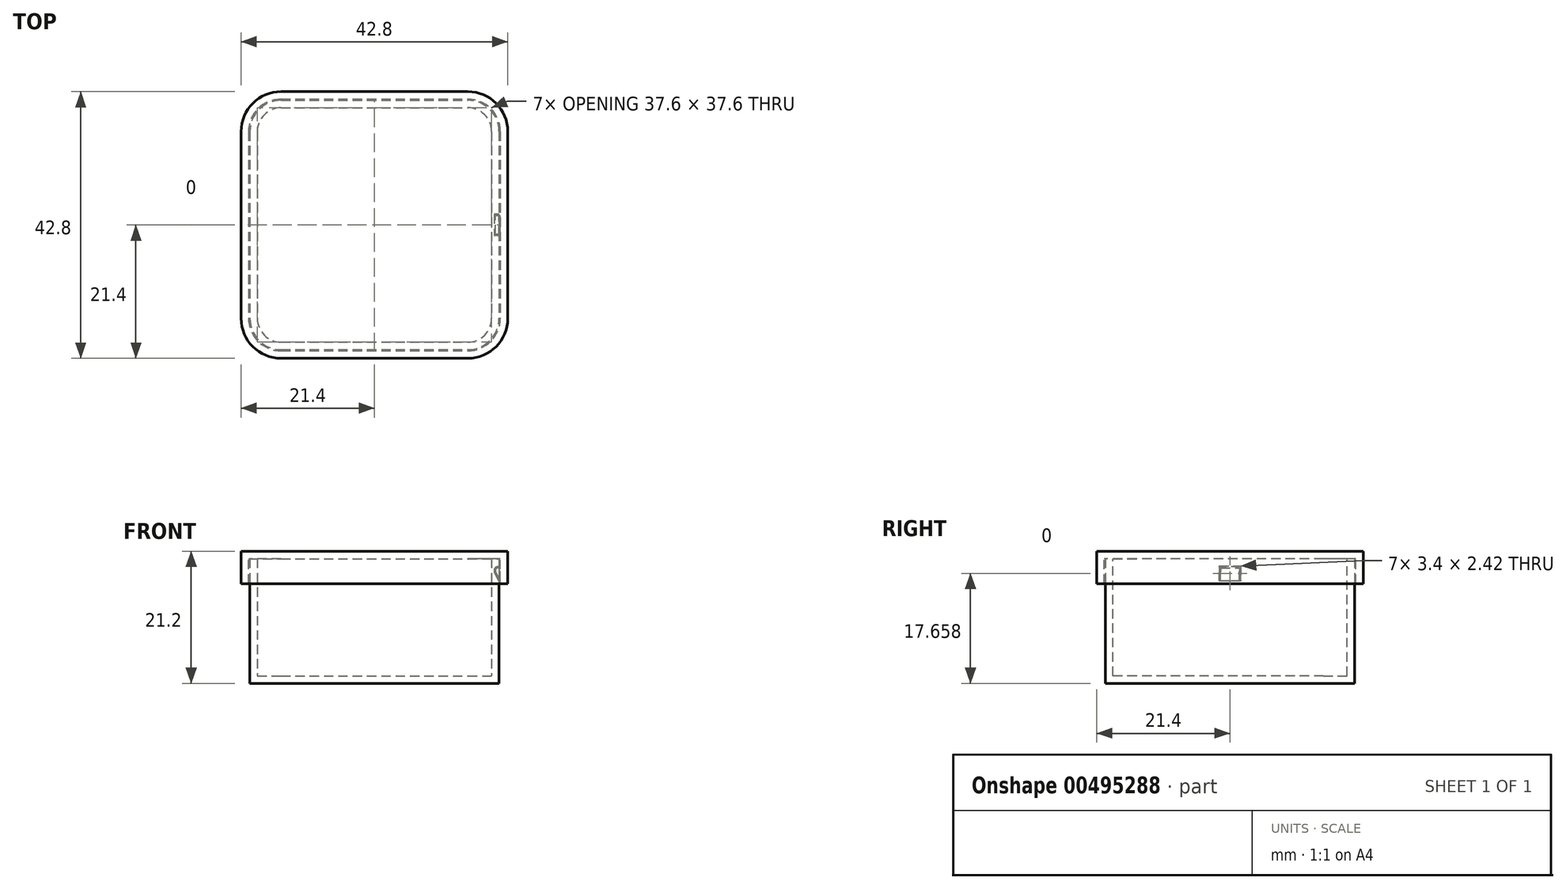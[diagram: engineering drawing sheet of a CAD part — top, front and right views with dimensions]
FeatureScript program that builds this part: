
annotation { "Feature Type Name" : "Feature", "Feature Type Description" : "" }
export const myFeature = defineFeature(function(context is Context, id is Id, definition is map)
    precondition{}
    {
        {
            var Q0;
            Q0=qCreatedBy(makeId("Top.planeOp"),FACE);
            var sketch = newSketch(context, id + "F0", { "sketchPlane" : qUnion([Q0])});
            skLineSegment(sketch, "E0.bottom", {"start": v(-20, 20) * mm, "end": v(20, 20) * mm});
            skLineSegment(sketch, "E0.top", {"start": v(-20, -20) * mm, "end": v(20, -20) * mm});
            skLineSegment(sketch, "E0.left", {"start": v(-20, 20) * mm, "end": v(-20, -20) * mm});
            skLineSegment(sketch, "E0.right", {"start": v(20, 20) * mm, "end": v(20, -20) * mm});
            skPoint(sketch, "E0.middle", {"position": v(0, 0) * mm});
            skSolve(sketch);
        }
        {
            var Q0;
            Q0=qSketchRegion(id+"F0",true);
            extrude(context, id + "F1", {"entities" : qUnion([Q0]), "depth" : 20 * mm});
        }
        {
            var Q0;
            Q0=makeQuery(id+"F1.opExtrude","SWEPT_EDGE",EDGE,{"disambiguationData":[OSD([sQuery(id+"F0.wireOp",EDGE,"E0.top"),sQuery(id+"F0.wireOp",EDGE,"E0.right")])]});
            var Q1;
            Q1=makeQuery(id+"F1.opExtrude","SWEPT_EDGE",EDGE,{"disambiguationData":[OSD([sQuery(id+"F0.wireOp",EDGE,"E0.bottom"),sQuery(id+"F0.wireOp",EDGE,"E0.right")])]});
            var Q2;
            Q2=makeQuery(id+"F1.opExtrude","SWEPT_EDGE",EDGE,{"disambiguationData":[OSD([sQuery(id+"F0.wireOp",EDGE,"E0.top"),sQuery(id+"F0.wireOp",EDGE,"E0.left")])]});
            var Q3;
            Q3=makeQuery(id+"F1.opExtrude","SWEPT_EDGE",EDGE,{"disambiguationData":[OSD([sQuery(id+"F0.wireOp",EDGE,"E0.bottom"),sQuery(id+"F0.wireOp",EDGE,"E0.left")])]});
            fillet(context, id + "F2", {"entities" : qUnion([Q0, Q1, Q2, Q3]), "radius" : 5 * mm, "tangentPropagation" : true, "allowEdgeOverflow" : false});
        }
        {
            var Q0;
            Q0=makeQuery(id+"F1.opExtrude","CAP_FACE",FACE,{"disambiguationData":[OSD([sQuery(id+"F0.wireOp",EDGE,"E0.bottom"),sQuery(id+"F0.wireOp",EDGE,"E0.top"),sQuery(id+"F0.wireOp",EDGE,"E0.left"),sQuery(id+"F0.wireOp",EDGE,"E0.right")])],"isStart":false});
            shell(context, id + "F3", {"entities" : qUnion([Q0]), "thickness" : 1.2 * mm});
        }
        {
            var Q0;
            Q0=makeQuery(id+"F1.opExtrude","CAP_FACE",FACE,{"disambiguationData":[OSD([sQuery(id+"F0.wireOp",EDGE,"E0.bottom"),sQuery(id+"F0.wireOp",EDGE,"E0.top"),sQuery(id+"F0.wireOp",EDGE,"E0.left"),sQuery(id+"F0.wireOp",EDGE,"E0.right")])],"isStart":false});
            var sketch = newSketch(context, id + "F4", { "sketchPlane" : qUnion([Q0])});
            skLineSegment(sketch, "E1.0", {"start": v(-15, -20) * mm, "end": v(15, -20) * mm});
            skArc(sketch, "E1.1", {"start": v(15, -20) * mm, "mid": v(18.54, -18.54) * mm, "end": v(20, -15) * mm});
            skLineSegment(sketch, "E1.2", {"start": v(20, 15) * mm, "end": v(20, -15) * mm});
            skArc(sketch, "E1.3", {"start": v(20, 15) * mm, "mid": v(18.54, 18.54) * mm, "end": v(15, 20) * mm});
            skLineSegment(sketch, "E1.4", {"start": v(-15, 20) * mm, "end": v(15, 20) * mm});
            skArc(sketch, "E1.5", {"start": v(-15, 20) * mm, "mid": v(-18.54, 18.54) * mm, "end": v(-20, 15) * mm});
            skLineSegment(sketch, "E1.6", {"start": v(-20, 15) * mm, "end": v(-20, -15) * mm});
            skArc(sketch, "E1.7", {"start": v(-20, -15) * mm, "mid": v(-18.54, -18.54) * mm, "end": v(-15, -20) * mm});
            skArc(sketch, "E2.0", {"start": v(-20.2, -15) * mm, "mid": v(-18.68, -18.68) * mm, "end": v(-15, -20.2) * mm});
            skLineSegment(sketch, "E2.1", {"start": v(-20.2, 15) * mm, "end": v(-20.2, -15) * mm});
            skLineSegment(sketch, "E2.2", {"start": v(-15, -20.2) * mm, "end": v(15, -20.2) * mm});
            skArc(sketch, "E2.3", {"start": v(-15, 20.2) * mm, "mid": v(-18.68, 18.68) * mm, "end": v(-20.2, 15) * mm});
            skArc(sketch, "E2.4", {"start": v(15, -20.2) * mm, "mid": v(18.68, -18.68) * mm, "end": v(20.2, -15) * mm});
            skLineSegment(sketch, "E2.5", {"start": v(20.2, 15) * mm, "end": v(20.2, -15) * mm});
            skArc(sketch, "E2.6", {"start": v(20.2, 15) * mm, "mid": v(18.68, 18.68) * mm, "end": v(15, 20.2) * mm});
            skLineSegment(sketch, "E2.7", {"start": v(-15, 20.2) * mm, "end": v(15, 20.2) * mm});
            skArc(sketch, "E3.0", {"start": v(-21.4, -15) * mm, "mid": v(-19.53, -19.53) * mm, "end": v(-15, -21.4) * mm});
            skLineSegment(sketch, "E3.1", {"start": v(-21.4, 15) * mm, "end": v(-21.4, -15) * mm});
            skLineSegment(sketch, "E3.2", {"start": v(-15, -21.4) * mm, "end": v(15, -21.4) * mm});
            skArc(sketch, "E3.3", {"start": v(-15, 21.4) * mm, "mid": v(-19.53, 19.53) * mm, "end": v(-21.4, 15) * mm});
            skArc(sketch, "E3.4", {"start": v(15, -21.4) * mm, "mid": v(19.53, -19.53) * mm, "end": v(21.4, -15) * mm});
            skLineSegment(sketch, "E3.5", {"start": v(21.4, 15) * mm, "end": v(21.4, -15) * mm});
            skArc(sketch, "E3.6", {"start": v(21.4, 15) * mm, "mid": v(19.53, 19.53) * mm, "end": v(15, 21.4) * mm});
            skLineSegment(sketch, "E3.7", {"start": v(-15, 21.4) * mm, "end": v(15, 21.4) * mm});
            skSolve(sketch);
        }
        {
            var Q0;
            Q0=makeQuery(id+"F4.imprint","IMPRINT",FACE,{"disambiguationData":[TD([[makeQuery(id+"F4.imprint","IMPRINT",EDGE,{"derivedFrom":sQuery(id+"F4.wireOp",EDGE,"E2.0")}),-1.0]])]});
            var Q1;
            {var subQ3=sQuery(id+"F0.wireOp",EDGE,"E0.bottom");Q1=makeQuery(id+"F4.imprint","IMPRINT",FACE,{"disambiguationData":[TD([[makeQuery(id+"F4.imprint","IMPRINT",EDGE,{"derivedFrom":makeQuery(id+"F3.opShell","OFFSET_EDGE",EDGE,{"disambiguationData":[OSD([subQ3]),TDD([makeQuery(id+"F1.opExtrude","CAP_EDGE",EDGE,{"disambiguationData":[OSD([subQ3])],"isStart":false})])]})}),-1.0]])]});}
            var Q2;
            Q2=makeQuery(id+"F4.imprint","IMPRINT",FACE,{"disambiguationData":[TD([[makeQuery(id+"F4.imprint","IMPRINT",EDGE,{"derivedFrom":sQuery(id+"F4.wireOp",EDGE,"E1.0")}),1.0]])]});
            var Q3;
            Q3=makeQuery(id+"F4.imprint","IMPRINT",FACE,{"disambiguationData":[TD([[makeQuery(id+"F4.imprint","IMPRINT",EDGE,{"derivedFrom":sQuery(id+"F4.wireOp",EDGE,"E1.0")}),-1.0]])]});
            extrude(context, id + "F5", {"entities" : qUnion([Q0, Q1, Q2, Q3]), "depth" : 1.2 * mm});
        }
        {
            var Q0;
            Q0=makeQuery(id+"F4.imprint","IMPRINT",FACE,{"disambiguationData":[TD([[makeQuery(id+"F4.imprint","IMPRINT",EDGE,{"derivedFrom":sQuery(id+"F4.wireOp",EDGE,"E2.0")}),-1.0]])]});
            extrude(context, id + "F6", {"entities" : qUnion([Q0]), "operationType" : NewBodyOperationType.ADD, "oppositeDirection" : true, "depth" : 4 * mm});
        }
        {
            var Q0;
            Q0=qCreatedBy(makeId("Front.planeOp"),FACE);
            var sketch = newSketch(context, id + "F7", { "sketchPlane" : qUnion([Q0])});
            skLineSegment(sketch, "E4", {"start": v(20.2, 16.5) * mm, "end": v(20.2, 18.5) * mm});
            skLineSegment(sketch, "E5", {"start": v(20.2, 18.5) * mm, "end": v(19.8, 18.5) * mm});
            skLineSegment(sketch, "E6", {"start": v(20.2, 16.5) * mm, "end": v(19.45, 17.91) * mm});
            skArc(sketch, "E7", {"start": v(19.8, 18.5) * mm, "mid": v(19.46, 18.3) * mm, "end": v(19.45, 17.91) * mm});
            skArc(sketch, "E8", {"start": v(19.8, 18.5) * mm, "mid": v(20.08, 18.62) * mm, "end": v(20.2, 18.9) * mm});
            skLineSegment(sketch, "E9", {"start": v(20.2, 18.5) * mm, "end": v(19.4, 18.5) * mm, "construction": true});
            skLineSegment(sketch, "E10", {"start": v(20.2, 18.5) * mm, "end": v(20.2, 18.9) * mm});
            skArc(sketch, "E11.0", {"start": v(19.8, 18.7) * mm, "mid": v(19.92, 18.74) * mm, "end": v(19.99, 18.84) * mm});
            skArc(sketch, "E11.1", {"start": v(19.8, 18.7) * mm, "mid": v(19.29, 18.4) * mm, "end": v(19.27, 17.82) * mm});
            skLineSegment(sketch, "E11.2", {"start": v(20.2, 16.08) * mm, "end": v(19.27, 17.82) * mm});
            skLineSegment(sketch, "E12", {"start": v(19.99, 18.84) * mm, "end": v(20.2, 19.45) * mm});
            skLineSegment(sketch, "E13", {"start": v(20.2, 18.9) * mm, "end": v(20.2, 20) * mm});
            skLineSegment(sketch, "E14", {"start": v(20.2, 16.5) * mm, "end": v(20.2, 16.08) * mm});
            skLineSegment(sketch, "E15.0.1", {"start": v(20.2, 20) * mm, "end": v(20.2, 16) * mm, "construction": true});
            skLineSegment(sketch, "E15.0.3", {"start": v(20.2, 16) * mm, "end": v(20.2, 20) * mm, "construction": true});
            skLineSegment(sketch, "E16.0", {"start": v(20, 20) * mm, "end": v(20, 0) * mm, "construction": true});
            skSolve(sketch);
        }
        {
            var Q0;
            Q0=makeQuery(id+"F7.imprint","IMPRINT",FACE,{"disambiguationData":[TD([[makeQuery(id+"F7.imprint","IMPRINT",EDGE,{"derivedFrom":sQuery(id+"F7.wireOp",EDGE,"E4")}),1.0]])]});
            var Q1;
            Q1=makeQuery(id+"F7.imprint","IMPRINT",FACE,{"disambiguationData":[TD([[makeQuery(id+"F7.imprint","IMPRINT",EDGE,{"derivedFrom":sQuery(id+"F7.wireOp",EDGE,"E5")}),-1.0]])]});
            var Q2;
            Q2=makeQuery(id+"F7.imprint","IMPRINT",FACE,{"disambiguationData":[TD([[makeQuery(id+"F7.imprint","IMPRINT",EDGE,{"derivedFrom":sQuery(id+"F7.wireOp",EDGE,"E6")}),1.0]])]});
            extrude(context, id + "F8", {"entities" : qUnion([Q0, Q1, Q2]), "operationType" : NewBodyOperationType.REMOVE, "endBound" : BoundingType.SYMMETRIC, "oppositeDirection" : true, "depth" : 3.4 * mm});
        }
        {
            var Q0;
            Q0=makeQuery(id+"F7.imprint","IMPRINT",FACE,{"disambiguationData":[TD([[makeQuery(id+"F7.imprint","IMPRINT",EDGE,{"derivedFrom":sQuery(id+"F7.wireOp",EDGE,"E4")}),1.0]])]});
            extrude(context, id + "F9", {"entities" : qUnion([Q0]), "operationType" : NewBodyOperationType.ADD, "endBound" : BoundingType.SYMMETRIC, "depth" : 3 * mm});
        }
        {
            var Q0;
            Q0=makeQuery(id+"F5.opExtrude","CAP_FACE",FACE,{"disambiguationData":[OSD([sQuery(id+"F4.wireOp",EDGE,"E3.0"),sQuery(id+"F4.wireOp",EDGE,"E3.1"),sQuery(id+"F4.wireOp",EDGE,"E3.2"),sQuery(id+"F4.wireOp",EDGE,"E3.3"),sQuery(id+"F4.wireOp",EDGE,"E3.4"),sQuery(id+"F4.wireOp",EDGE,"E3.5"),sQuery(id+"F4.wireOp",EDGE,"E3.6"),sQuery(id+"F4.wireOp",EDGE,"E3.7")])],"isStart":false});
            var sketch = newSketch(context, id + "F10", { "sketchPlane" : qUnion([Q0])});
            skCircle(sketch, "E17", {"center": v(0, 0) * mm, "radius": 21.4 * mm, "construction": true});
            skSolve(sketch);
        }
    });
